# Revit family: 210_d95d6a5261934f72974ca134284f48
name_source: partatom
category: Mechanical Equipment
revit_build: Autodesk Revit 2018 (Build: 20170223_1515(x64)
units: mm (PartAtom-declared; Revit-internal decimal feet)

## family parameters
Always vertical = Yes
Classification = None
Cut with Voids When Loaded = No
Part Type = Breaks Into
Room Calculation Point = No
Round Connector Dimension = Use Diameter
Shared = No
Work Plane-Based = No

## types (3) — shared parameters
Description = Roof fan DVA ECC
Manufacturer = Flexit
QmdConnectorList = 201;D;201;D
URL = www.flexit.no
W = 500 mm  [stored 1.64042 ft]
magiPartTypeId = 210
magiProductFamilyId = d95d6a5261934f72974ca134284f48

## per-type parameters (varying)
| type | D | L | SW2 | X1 | X2 | X3 | Y1 | Y2 | Y3 | Z1 | Z2 | Z3 | Z4 | Z5 | magiProductId |
| 180-115772 | 180 mm | 337 mm  [stored 1.10564 ft] | Yes | 152 mm | 194 mm  [stored 0.636483 ft] | 175 mm | 63 mm | 80 mm | 72 mm | 19 mm  [stored 0.062336 ft] | 48 mm | 10 mm  [stored 0.0328084 ft] | 8 mm  [stored 0.0262467 ft] | 106 mm | e121d953e08944e3bc3988647507a3 |
| 250-115773 | 250 mm | 437 mm  [stored 1.43373 ft] | No | 197 mm | 271 mm | 243 mm | 81 mm | 112 mm | 101 mm | 25 mm  [stored 0.082021 ft] | 62 mm | 12 mm  [stored 0.0393701 ft] | 10 mm  [stored 0.0328084 ft] | 139 mm | b06c640c768840d2b1add921a364a6 |
| 400-115774 | 400 mm | 598 mm  [stored 1.96194 ft] | No | 269 mm | 373 mm | 335 mm | 111 mm | 154 mm | 139 mm | 33 mm | 83 mm | 17 mm | 13 mm | 186 mm | 138a5e8a982a4ab09fea2063c558df |

note: column(s) folded — value = type name in every type: MC Product Code

note: [stored X ft] marks values corroborated as IEEE doubles in the binary element streams (Revit-internal decimal feet)
